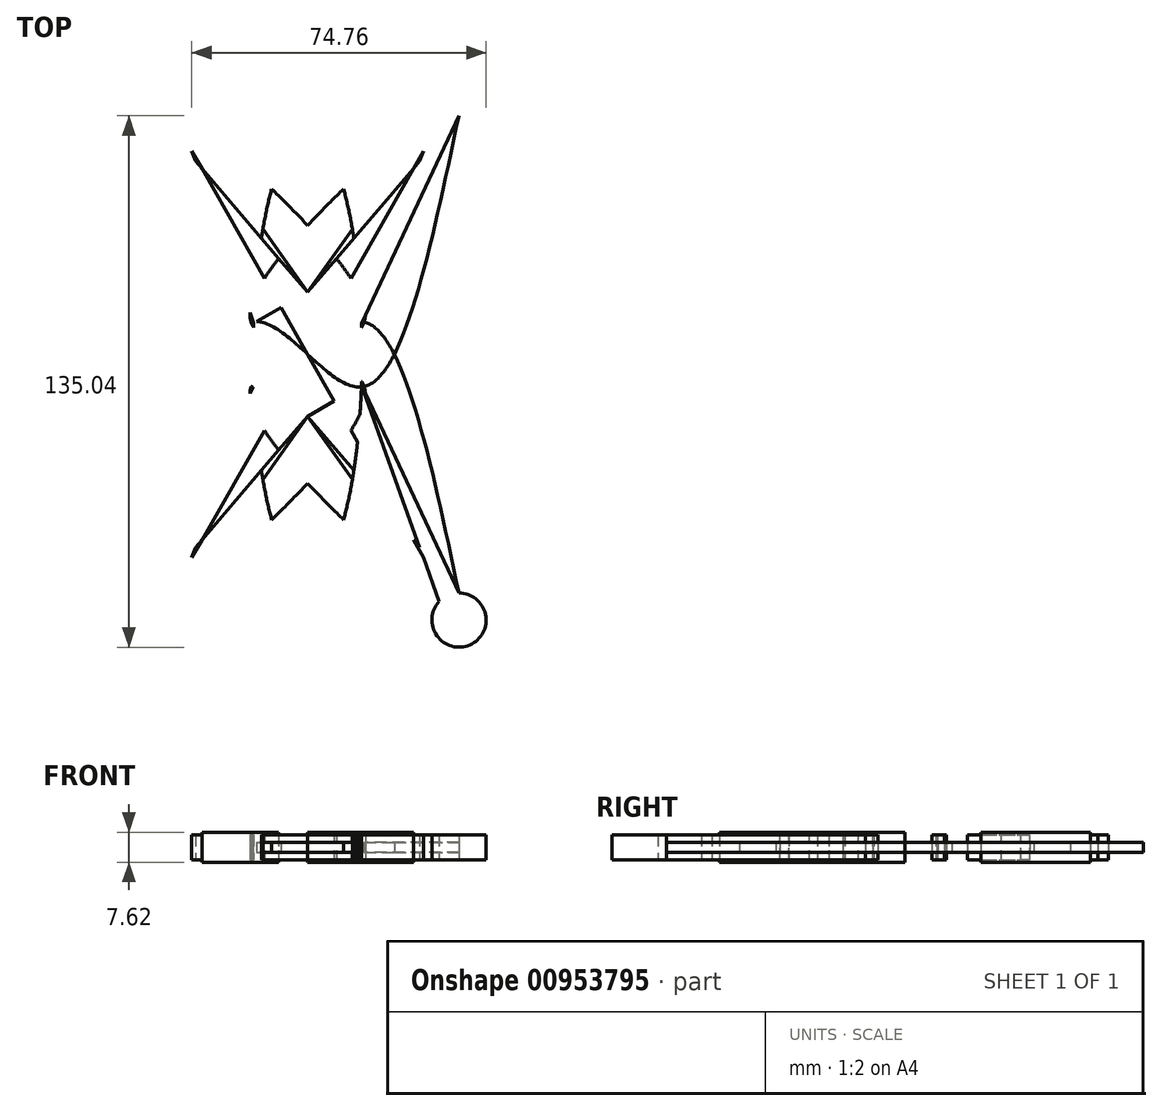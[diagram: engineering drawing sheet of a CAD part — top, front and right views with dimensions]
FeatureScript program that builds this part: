
annotation { "Feature Type Name" : "Feature", "Feature Type Description" : "" }
export const myFeature = defineFeature(function(context is Context, id is Id, definition is map)
    precondition{}
    {
        {
            var Q0;
            Q0=qCreatedBy(makeId("Top.planeOp"),FACE);
            var sketch = newSketch(context, id + "F0", { "sketchPlane" : qUnion([Q0])});
            skEllipse(sketch, "E0", {"center": v(0, 0) * mm, "majorRadius": 55.88 * mm, "minorRadius": 13.83 * mm, "majorAxis": v(0, 1)});
            skCircle(sketch, "E1.cCircle", {"center": v(0, 0) * mm, "radius": 13.7 * mm, "construction": true});
            skLineSegment(sketch, "E1.0", {"start": v(0, 15.8) * mm, "end": v(13.7, 7.9) * mm});
            skLineSegment(sketch, "E1.1", {"start": v(13.7, 7.9) * mm, "end": v(13.7, -7.9) * mm});
            skLineSegment(sketch, "E1.2", {"start": v(13.7, -7.9) * mm, "end": v(0, -15.8) * mm});
            skLineSegment(sketch, "E1.3", {"start": v(0, -15.8) * mm, "end": v(-13.7, -7.9) * mm});
            skLineSegment(sketch, "E1.4", {"start": v(-13.7, -7.9) * mm, "end": v(-13.7, 7.9) * mm});
            skLineSegment(sketch, "E1.5", {"start": v(-13.7, 7.9) * mm, "end": v(0, 15.8) * mm});
            skPoint(sketch, "E1.0.midPoint", {"position": v(6.85, 11.86) * mm});
            skLineSegment(sketch, "E2", {"start": v(0, 15.8) * mm, "end": v(-33.42, 62.8) * mm});
            skLineSegment(sketch, "E3", {"start": v(-13.7, 7.9) * mm, "end": v(-33.42, 62.8) * mm});
            skLineSegment(sketch, "E4", {"start": v(0, 15.8) * mm, "end": v(-38.4, 60.63) * mm});
            skLineSegment(sketch, "E5", {"start": v(-38.4, 60.63) * mm, "end": v(-13.7, 7.9) * mm});
            skLineSegment(sketch, "E6.MirrorCS", {"start": v(38.4, 60.63) * mm, "end": v(13.7, 7.9) * mm});
            skLineSegment(sketch, "E7.MirrorCS", {"start": v(0, 15.8) * mm, "end": v(38.4, 60.63) * mm});
            skLineSegment(sketch, "E8.MirrorCS", {"start": v(13.7, 7.9) * mm, "end": v(33.42, 62.8) * mm});
            skLineSegment(sketch, "E9.MirrorCS", {"start": v(13.7, 7.9) * mm, "end": v(0, 15.8) * mm});
            skLineSegment(sketch, "E10.MirrorCS", {"start": v(0, 15.8) * mm, "end": v(33.42, 62.8) * mm});
            skLineSegment(sketch, "E11.MirrorCS", {"start": v(-13.7, 7.9) * mm, "end": v(-13.7, -7.9) * mm});
            skLineSegment(sketch, "E12.MirrorCS", {"start": v(13.7, -7.9) * mm, "end": v(13.7, 7.9) * mm});
            skLineSegment(sketch, "E13.MirrorCS", {"start": v(0, 15.8) * mm, "end": v(-13.7, 7.9) * mm});
            skPoint(sketch, "E14.MirrorP", {"position": v(-6.85, 11.86) * mm});
            skEllipse(sketch, "E15.MirrorC", {"center": v(0, 0) * mm, "majorRadius": 55.88 * mm, "minorRadius": 13.83 * mm, "majorAxis": v(0, 1)});
            skLineSegment(sketch, "E16.MirrorCS", {"start": v(-13.7, -7.9) * mm, "end": v(0, -15.8) * mm});
            skLineSegment(sketch, "E17.MirrorCS", {"start": v(0, -15.8) * mm, "end": v(-38.4, -60.63) * mm});
            skLineSegment(sketch, "E18.MirrorCS", {"start": v(-13.7, -7.9) * mm, "end": v(-33.42, -62.8) * mm});
            skLineSegment(sketch, "E19.MirrorCS", {"start": v(0, -15.8) * mm, "end": v(-33.42, -62.8) * mm});
            skLineSegment(sketch, "E20.MirrorCS", {"start": v(-38.4, -60.63) * mm, "end": v(-13.7, -7.9) * mm});
            skPoint(sketch, "E21.MirrorP", {"position": v(-6.85, -11.86) * mm});
            skEllipse(sketch, "E22.MirrorC", {"center": v(0, 0) * mm, "majorRadius": 55.88 * mm, "minorRadius": 13.83 * mm, "majorAxis": v(0, -1)});
            skEllipse(sketch, "E23.MirrorC", {"center": v(0, 0) * mm, "majorRadius": 55.88 * mm, "minorRadius": 13.83 * mm, "majorAxis": v(0, -1)});
            skLineSegment(sketch, "E24.MirrorCS", {"start": v(0, -15.8) * mm, "end": v(13.7, -7.9) * mm});
            skLineSegment(sketch, "E25.MirrorCS", {"start": v(13.7, -7.9) * mm, "end": v(33.42, -62.8) * mm});
            skLineSegment(sketch, "E26.MirrorCS", {"start": v(38.4, -60.63) * mm, "end": v(13.7, -7.9) * mm});
            skLineSegment(sketch, "E27.MirrorCS", {"start": v(0, -15.8) * mm, "end": v(33.42, -62.8) * mm});
            skLineSegment(sketch, "E28.MirrorCS", {"start": v(0, -15.8) * mm, "end": v(38.4, -60.63) * mm});
            skPoint(sketch, "E29.MirrorP", {"position": v(6.85, -11.86) * mm});
            skEllipse(sketch, "E30.MirrorC", {"center": v(0, 0) * mm, "majorRadius": 55.88 * mm, "minorRadius": 13.83 * mm, "majorAxis": v(0, -1)});
            skEllipse(sketch, "E31.MirrorC", {"center": v(0, 0) * mm, "majorRadius": 55.88 * mm, "minorRadius": 13.83 * mm, "majorAxis": v(0, 1)});
            skEllipse(sketch, "E32.MirrorC", {"center": v(0, 0) * mm, "majorRadius": 55.88 * mm, "minorRadius": 13.83 * mm, "majorAxis": v(0, -1)});
            skEllipse(sketch, "E33.MirrorC", {"center": v(0, 0) * mm, "majorRadius": 55.88 * mm, "minorRadius": 13.83 * mm, "majorAxis": v(0, 1)});
            skArc(sketch, "E34", {"start": v(-38.4, -60.63) * mm, "mid": v(-41.21, -73.83) * mm, "end": v(-33.42, -62.8) * mm});
            skArc(sketch, "E35.MirrorCS", {"start": v(-38.4, 60.63) * mm, "mid": v(-41.21, 73.83) * mm, "end": v(-33.42, 62.8) * mm});
            skArc(sketch, "E36.MirrorCS", {"start": v(38.4, 60.63) * mm, "mid": v(41.21, 73.83) * mm, "end": v(33.42, 62.8) * mm});
            skArc(sketch, "E37.MirrorCS", {"start": v(38.4, -60.63) * mm, "mid": v(41.21, -73.83) * mm, "end": v(33.42, -62.8) * mm});
            skEllipse(sketch, "E38.MirrorC", {"center": v(0, 0) * mm, "majorRadius": 55.88 * mm, "minorRadius": 13.83 * mm, "majorAxis": v(0, -1)});
            skFitSpline(sketch, "E39", {"points": [v(0, 0) * mm, v(15.27, 7.9) * mm, v(38.4, -60.63) * mm], "startDerivative": vector(48.6, 44.78) * mm, "endDerivative": vector(30.3, -144.32) * mm});
            skFitSpline(sketch, "E40.MirrorCS", {"points": [v(0, 0) * mm, v(15.27, -7.9) * mm, v(38.4, 60.63) * mm], "startDerivative": vector(48.6, -44.78) * mm, "endDerivative": vector(30.3, 144.32) * mm});
            skFitSpline(sketch, "E41.MirrorCS", {"points": [v(0, 0) * mm, v(-15.27, -7.9) * mm, v(-38.4, 60.63) * mm], "startDerivative": vector(-48.6, -44.78) * mm, "endDerivative": vector(-30.3, 144.32) * mm});
            skFitSpline(sketch, "E42.MirrorCS", {"points": [v(0, 0) * mm, v(-15.27, 7.9) * mm, v(-38.4, -60.63) * mm], "startDerivative": vector(-48.6, 44.78) * mm, "endDerivative": vector(-30.3, -144.32) * mm});
            skLineSegment(sketch, "E43", {"start": v(0, 0) * mm, "end": v(-38.45, -67.52) * mm});
            skFitSpline(sketch, "E44.MirrorCS", {"points": [v(0, 0) * mm, v(-15.27, -7.9) * mm, v(-38.4, 60.63) * mm], "startDerivative": vector(-48.6, -44.78) * mm, "endDerivative": vector(-30.3, 144.32) * mm});
            skFitSpline(sketch, "E45.MirrorCS", {"points": [v(0, 0) * mm, v(-15.27, -7.9) * mm, v(-38.4, 60.63) * mm], "startDerivative": vector(-48.6, -44.78) * mm, "endDerivative": vector(-30.3, 144.32) * mm});
            skFitSpline(sketch, "E46.MirrorCS", {"points": [v(0, 0) * mm, v(14.6, -9.1) * mm, v(-32.55, -63.96) * mm], "startDerivative": vector(63.3, -18.95) * mm, "endDerivative": vector(-108.66, -99.7) * mm});
            skLineSegment(sketch, "E47.MirrorCS", {"start": v(0, 0) * mm, "end": v(38.45, -67.52) * mm});
            skFitSpline(sketch, "E48.MirrorCS", {"points": [v(0, 0) * mm, v(-14.6, -9.1) * mm, v(32.55, -63.96) * mm], "startDerivative": vector(-63.3, -18.95) * mm, "endDerivative": vector(108.66, -99.7) * mm});
            skLineSegment(sketch, "E49", {"start": v(0, 0) * mm, "end": v(38.45, 67.52) * mm});
            skLineSegment(sketch, "E50", {"start": v(-38.45, 67.52) * mm, "end": v(0, 0) * mm});
            skFitSpline(sketch, "E51.MirrorCS", {"points": [v(0, 0) * mm, v(-14.6, 9.1) * mm, v(32.55, 63.96) * mm], "startDerivative": vector(-63.3, 18.95) * mm, "endDerivative": vector(108.66, 99.7) * mm});
            skFitSpline(sketch, "E52.MirrorCS", {"points": [v(0, 0) * mm, v(14.6, 9.1) * mm, v(-32.55, 63.96) * mm], "startDerivative": vector(63.3, 18.95) * mm, "endDerivative": vector(-108.66, 99.7) * mm});
            skSolve(sketch);
        }
        {
            var Q0;
            {var subQ0=sQuery(id+"F0.wireOp",EDGE,"E45.MirrorCS");var subQ5=sQuery(id+"F0.wireOp",EDGE,"E42.MirrorCS");var subQ6=makeQuery(id+"F0.imprint","INTERSECT",VERTEX,{"derivedFrom":[subQ5,subQ0]});Q0=makeQuery(id+"F0.imprint","IMPRINT",FACE,{"disambiguationData":[TD([[makeQuery(id+"F0.imprint","IMPRINT",EDGE,{"disambiguationData":[TD([[subQ6,1.0]])],"derivedFrom":subQ5}),-1.0]])]});}
            var Q1;
            {var subQ3=sQuery(id+"F0.wireOp",EDGE,"E38.MirrorC");var subQ5=sQuery(id+"F0.wireOp",EDGE,"E52.MirrorCS");var subQ7=makeQuery(id+"F0.imprint","INTERSECT",VERTEX,{"disambiguationData":[OD(0.0)],"derivedFrom":[subQ3,subQ5]});Q1=makeQuery(id+"F0.imprint","IMPRINT",FACE,{"disambiguationData":[TD([[makeQuery(id+"F0.imprint","IMPRINT",EDGE,{"disambiguationData":[TD([[subQ7,-1.0]])],"derivedFrom":subQ3}),-1.0]])]});}
            var Q2;
            {var subQ3=sQuery(id+"F0.wireOp",EDGE,"E38.MirrorC");var subQ5=sQuery(id+"F0.wireOp",EDGE,"E51.MirrorCS");var subQ7=makeQuery(id+"F0.imprint","INTERSECT",VERTEX,{"disambiguationData":[OD(0.0)],"derivedFrom":[subQ3,subQ5]});Q2=makeQuery(id+"F0.imprint","IMPRINT",FACE,{"disambiguationData":[TD([[makeQuery(id+"F0.imprint","IMPRINT",EDGE,{"disambiguationData":[TD([[subQ7,1.0]])],"derivedFrom":subQ3}),-1.0]])]});}
            var Q3;
            {var subQ0=sQuery(id+"F0.wireOp",EDGE,"E40.MirrorCS");var subQ5=sQuery(id+"F0.wireOp",EDGE,"E39");var subQ6=makeQuery(id+"F0.imprint","INTERSECT",VERTEX,{"derivedFrom":[subQ0,subQ5]});Q3=makeQuery(id+"F0.imprint","IMPRINT",FACE,{"disambiguationData":[TD([[makeQuery(id+"F0.imprint","IMPRINT",EDGE,{"disambiguationData":[TD([[subQ6,1.0]])],"derivedFrom":subQ5}),1.0]])]});}
            var Q4;
            {var subQ0=sQuery(id+"F0.wireOp",EDGE,"E39");var subQ5=sQuery(id+"F0.wireOp",EDGE,"E40.MirrorCS");var subQ6=makeQuery(id+"F0.imprint","INTERSECT",VERTEX,{"derivedFrom":[subQ5,subQ0]});Q4=makeQuery(id+"F0.imprint","IMPRINT",FACE,{"disambiguationData":[TD([[makeQuery(id+"F0.imprint","IMPRINT",EDGE,{"disambiguationData":[TD([[subQ6,1.0]])],"derivedFrom":subQ5}),-1.0]])]});}
            var Q5;
            {var subQ3=sQuery(id+"F0.wireOp",EDGE,"E38.MirrorC");var subQ5=sQuery(id+"F0.wireOp",EDGE,"E48.MirrorCS");var subQ7=makeQuery(id+"F0.imprint","INTERSECT",VERTEX,{"disambiguationData":[OD(0.0)],"derivedFrom":[subQ3,subQ5]});Q5=makeQuery(id+"F0.imprint","IMPRINT",FACE,{"disambiguationData":[TD([[makeQuery(id+"F0.imprint","IMPRINT",EDGE,{"disambiguationData":[TD([[subQ7,-1.0]])],"derivedFrom":subQ3}),-1.0]])]});}
            var Q6;
            {var subQ3=sQuery(id+"F0.wireOp",EDGE,"E38.MirrorC");var subQ5=sQuery(id+"F0.wireOp",EDGE,"E46.MirrorCS");var subQ7=makeQuery(id+"F0.imprint","INTERSECT",VERTEX,{"disambiguationData":[OD(0.0)],"derivedFrom":[subQ3,subQ5]});Q6=makeQuery(id+"F0.imprint","IMPRINT",FACE,{"disambiguationData":[TD([[makeQuery(id+"F0.imprint","IMPRINT",EDGE,{"disambiguationData":[TD([[subQ7,1.0]])],"derivedFrom":subQ3}),-1.0]])]});}
            var Q7;
            {var subQ0=sQuery(id+"F0.wireOp",EDGE,"E42.MirrorCS");var subQ5=sQuery(id+"F0.wireOp",EDGE,"E45.MirrorCS");var subQ6=makeQuery(id+"F0.imprint","INTERSECT",VERTEX,{"derivedFrom":[subQ0,subQ5]});Q7=makeQuery(id+"F0.imprint","IMPRINT",FACE,{"disambiguationData":[TD([[makeQuery(id+"F0.imprint","IMPRINT",EDGE,{"disambiguationData":[TD([[subQ6,1.0]])],"derivedFrom":subQ5}),1.0]])]});}
            var Q8;
            {var subQ0=sQuery(id+"F0.wireOp",EDGE,"E48.MirrorCS");var subQ1=sQuery(id+"F0.wireOp",EDGE,"E38.MirrorC");var subQ2=makeQuery(id+"F0.imprint","INTERSECT",VERTEX,{"disambiguationData":[OD(0.0)],"derivedFrom":[subQ1,subQ0]});Q8=makeQuery(id+"F0.imprint","IMPRINT",FACE,{"disambiguationData":[TD([[makeQuery(id+"F0.imprint","IMPRINT",EDGE,{"disambiguationData":[TD([[subQ2,1.0]])],"derivedFrom":subQ1}),1.0]])]});}
            var Q9;
            {var subQ0=sQuery(id+"F0.wireOp",EDGE,"E51.MirrorCS");var subQ1=sQuery(id+"F0.wireOp",EDGE,"E38.MirrorC");var subQ2=makeQuery(id+"F0.imprint","INTERSECT",VERTEX,{"disambiguationData":[OD(0.0)],"derivedFrom":[subQ1,subQ0]});Q9=makeQuery(id+"F0.imprint","IMPRINT",FACE,{"disambiguationData":[TD([[makeQuery(id+"F0.imprint","IMPRINT",EDGE,{"disambiguationData":[TD([[subQ2,-1.0]])],"derivedFrom":subQ1}),1.0]])]});}
            var Q10;
            {var subQ0=sQuery(id+"F0.wireOp",EDGE,"E51.MirrorCS");var subQ1=sQuery(id+"F0.wireOp",EDGE,"E2");var subQ2=makeQuery(id+"F0.imprint","INTERSECT",VERTEX,{"derivedFrom":[subQ1,subQ0]});Q10=makeQuery(id+"F0.imprint","IMPRINT",FACE,{"disambiguationData":[TD([[makeQuery(id+"F0.imprint","IMPRINT",EDGE,{"disambiguationData":[TD([[subQ2,-1.0]])],"derivedFrom":subQ1}),-1.0]])]});}
            var Q11;
            {var subQ0=sQuery(id+"F0.wireOp",EDGE,"E52.MirrorCS");var subQ1=sQuery(id+"F0.wireOp",EDGE,"E10.MirrorCS");var subQ2=makeQuery(id+"F0.imprint","INTERSECT",VERTEX,{"derivedFrom":[subQ1,subQ0]});Q11=makeQuery(id+"F0.imprint","IMPRINT",FACE,{"disambiguationData":[TD([[makeQuery(id+"F0.imprint","IMPRINT",EDGE,{"disambiguationData":[TD([[subQ2,-1.0]])],"derivedFrom":subQ1}),1.0]])]});}
            var Q12;
            {var subQ0=sQuery(id+"F0.wireOp",EDGE,"E48.MirrorCS");var subQ1=sQuery(id+"F0.wireOp",EDGE,"E19.MirrorCS");var subQ2=makeQuery(id+"F0.imprint","INTERSECT",VERTEX,{"derivedFrom":[subQ1,subQ0]});Q12=makeQuery(id+"F0.imprint","IMPRINT",FACE,{"disambiguationData":[TD([[makeQuery(id+"F0.imprint","IMPRINT",EDGE,{"disambiguationData":[TD([[subQ2,-1.0]])],"derivedFrom":subQ1}),1.0]])]});}
            var Q13;
            {var subQ0=sQuery(id+"F0.wireOp",EDGE,"E46.MirrorCS");var subQ1=sQuery(id+"F0.wireOp",EDGE,"E27.MirrorCS");var subQ2=makeQuery(id+"F0.imprint","INTERSECT",VERTEX,{"derivedFrom":[subQ1,subQ0]});Q13=makeQuery(id+"F0.imprint","IMPRINT",FACE,{"disambiguationData":[TD([[makeQuery(id+"F0.imprint","IMPRINT",EDGE,{"disambiguationData":[TD([[subQ2,-1.0]])],"derivedFrom":subQ1}),-1.0]])]});}
            var Q14;
            {var subQ0=sQuery(id+"F0.wireOp",EDGE,"E27.MirrorCS");var subQ5=sQuery(id+"F0.wireOp",EDGE,"E46.MirrorCS");var subQ6=makeQuery(id+"F0.imprint","INTERSECT",VERTEX,{"derivedFrom":[subQ0,subQ5]});Q14=makeQuery(id+"F0.imprint","IMPRINT",FACE,{"disambiguationData":[TD([[makeQuery(id+"F0.imprint","IMPRINT",EDGE,{"disambiguationData":[TD([[subQ6,-1.0]])],"derivedFrom":subQ5}),-1.0]])]});}
            var Q15;
            {var subQ0=sQuery(id+"F0.wireOp",EDGE,"E2");var subQ5=sQuery(id+"F0.wireOp",EDGE,"E51.MirrorCS");var subQ6=makeQuery(id+"F0.imprint","INTERSECT",VERTEX,{"derivedFrom":[subQ0,subQ5]});Q15=makeQuery(id+"F0.imprint","IMPRINT",FACE,{"disambiguationData":[TD([[makeQuery(id+"F0.imprint","IMPRINT",EDGE,{"disambiguationData":[TD([[subQ6,-1.0]])],"derivedFrom":subQ5}),-1.0]])]});}
            extrude(context, id + "F1", {"entities" : qUnion([Q0, Q1, Q2, Q3, Q4, Q5, Q6, Q7, Q8, Q9, Q10, Q11, Q12, Q13, Q14, Q15]), "endBound" : BoundingType.SYMMETRIC, "depth" : 2.54 * mm, "offsetDistance" : 25.4 * mm});
        }
        {
            var Q0;
            {var subQ4=sQuery(id+"F0.wireOp",EDGE,"E3");var subQ7=makeQuery(id+"F0.imprint","INTERSECT",VERTEX,{"derivedFrom":[subQ4,sQuery(id+"F0.wireOp",EDGE,"E50")]});Q0=makeQuery(id+"F0.imprint","IMPRINT",FACE,{"disambiguationData":[TD([[makeQuery(id+"F0.imprint","IMPRINT",EDGE,{"disambiguationData":[TD([[subQ7,1.0]])],"derivedFrom":subQ4}),1.0]])]});}
            var Q1;
            {var subQ3=sQuery(id+"F0.wireOp",EDGE,"E51.MirrorCS");var subQ5=sQuery(id+"F0.wireOp",EDGE,"E3");var subQ6=makeQuery(id+"F0.imprint","INTERSECT",VERTEX,{"derivedFrom":[subQ5,subQ3]});Q1=makeQuery(id+"F0.imprint","IMPRINT",FACE,{"disambiguationData":[TD([[makeQuery(id+"F0.imprint","IMPRINT",EDGE,{"disambiguationData":[TD([[subQ6,-1.0]])],"derivedFrom":subQ5}),1.0]])]});}
            var Q2;
            {var subQ0=sQuery(id+"F0.wireOp",EDGE,"E38.MirrorC");var subQ1=sQuery(id+"F0.wireOp",EDGE,"E4");var subQ2=makeQuery(id+"F0.imprint","INTERSECT",VERTEX,{"derivedFrom":[subQ1,subQ0]});Q2=makeQuery(id+"F0.imprint","IMPRINT",FACE,{"disambiguationData":[TD([[makeQuery(id+"F0.imprint","IMPRINT",EDGE,{"disambiguationData":[TD([[subQ2,-1.0]])],"derivedFrom":subQ1}),-1.0]])]});}
            var Q3;
            {var subQ3=sQuery(id+"F0.wireOp",EDGE,"E8.MirrorCS");var subQ6=makeQuery(id+"F0.imprint","INTERSECT",VERTEX,{"derivedFrom":[subQ3,sQuery(id+"F0.wireOp",EDGE,"E49")]});Q3=makeQuery(id+"F0.imprint","IMPRINT",FACE,{"disambiguationData":[TD([[makeQuery(id+"F0.imprint","IMPRINT",EDGE,{"disambiguationData":[TD([[subQ6,1.0]])],"derivedFrom":subQ3}),-1.0]])]});}
            var Q4;
            {var subQ0=sQuery(id+"F0.wireOp",EDGE,"E38.MirrorC");var subQ1=sQuery(id+"F0.wireOp",EDGE,"E7.MirrorCS");var subQ2=makeQuery(id+"F0.imprint","INTERSECT",VERTEX,{"derivedFrom":[subQ1,subQ0]});Q4=makeQuery(id+"F0.imprint","IMPRINT",FACE,{"disambiguationData":[TD([[makeQuery(id+"F0.imprint","IMPRINT",EDGE,{"disambiguationData":[TD([[subQ2,-1.0]])],"derivedFrom":subQ1}),1.0]])]});}
            var Q5;
            {var subQ0=sQuery(id+"F0.wireOp",EDGE,"E52.MirrorCS");var subQ1=sQuery(id+"F0.wireOp",EDGE,"E8.MirrorCS");var subQ2=makeQuery(id+"F0.imprint","INTERSECT",VERTEX,{"derivedFrom":[subQ1,subQ0]});Q5=makeQuery(id+"F0.imprint","IMPRINT",FACE,{"disambiguationData":[TD([[makeQuery(id+"F0.imprint","IMPRINT",EDGE,{"disambiguationData":[TD([[subQ2,-1.0]])],"derivedFrom":subQ1}),-1.0]])]});}
            var Q6;
            {var subQ1=sQuery(id+"F0.wireOp",EDGE,"E28.MirrorCS");var subQ3=sQuery(id+"F0.wireOp",EDGE,"E25.MirrorCS");var subQ4=makeQuery(id+"F0.imprint","INTERSECT",VERTEX,{"derivedFrom":[subQ1,subQ3]});Q6=makeQuery(id+"F0.imprint","IMPRINT",FACE,{"disambiguationData":[TD([[makeQuery(id+"F0.imprint","IMPRINT",EDGE,{"disambiguationData":[TD([[subQ4,1.0]])],"derivedFrom":subQ3}),1.0]])]});}
            var Q7;
            {var subQ0=sQuery(id+"F0.wireOp",EDGE,"E38.MirrorC");var subQ1=sQuery(id+"F0.wireOp",EDGE,"E28.MirrorCS");var subQ2=makeQuery(id+"F0.imprint","INTERSECT",VERTEX,{"derivedFrom":[subQ1,subQ0]});Q7=makeQuery(id+"F0.imprint","IMPRINT",FACE,{"disambiguationData":[TD([[makeQuery(id+"F0.imprint","IMPRINT",EDGE,{"disambiguationData":[TD([[subQ2,-1.0]])],"derivedFrom":subQ1}),-1.0]])]});}
            var Q8;
            {var subQ3=sQuery(id+"F0.wireOp",EDGE,"E38.MirrorC");var subQ5=sQuery(id+"F0.wireOp",EDGE,"E17.MirrorCS");var subQ6=makeQuery(id+"F0.imprint","INTERSECT",VERTEX,{"derivedFrom":[subQ5,subQ3]});Q8=makeQuery(id+"F0.imprint","IMPRINT",FACE,{"disambiguationData":[TD([[makeQuery(id+"F0.imprint","IMPRINT",EDGE,{"disambiguationData":[TD([[subQ6,-1.0]])],"derivedFrom":subQ5}),1.0]])]});}
            var Q9;
            {var subQ0=sQuery(id+"F0.wireOp",EDGE,"E48.MirrorCS");var subQ1=sQuery(id+"F0.wireOp",EDGE,"E18.MirrorCS");var subQ2=makeQuery(id+"F0.imprint","INTERSECT",VERTEX,{"derivedFrom":[subQ1,subQ0]});Q9=makeQuery(id+"F0.imprint","IMPRINT",FACE,{"disambiguationData":[TD([[makeQuery(id+"F0.imprint","IMPRINT",EDGE,{"disambiguationData":[TD([[subQ2,-1.0]])],"derivedFrom":subQ1}),-1.0]])]});}
            var Q10;
            {var subQ0=sQuery(id+"F0.wireOp",EDGE,"E43");var subQ1=sQuery(id+"F0.wireOp",EDGE,"E18.MirrorCS");var subQ2=makeQuery(id+"F0.imprint","INTERSECT",VERTEX,{"derivedFrom":[subQ1,subQ0]});Q10=makeQuery(id+"F0.imprint","IMPRINT",FACE,{"disambiguationData":[TD([[makeQuery(id+"F0.imprint","IMPRINT",EDGE,{"disambiguationData":[TD([[subQ2,1.0]])],"derivedFrom":subQ1}),1.0]])]});}
            var Q11;
            {var subQ0=sQuery(id+"F0.wireOp",EDGE,"E48.MirrorCS");var subQ1=sQuery(id+"F0.wireOp",EDGE,"E17.MirrorCS");var subQ2=makeQuery(id+"F0.imprint","INTERSECT",VERTEX,{"derivedFrom":[subQ1,subQ0]});Q11=makeQuery(id+"F0.imprint","IMPRINT",FACE,{"disambiguationData":[TD([[makeQuery(id+"F0.imprint","IMPRINT",EDGE,{"disambiguationData":[TD([[subQ2,-1.0]])],"derivedFrom":subQ1}),1.0]])]});}
            var Q12;
            {var subQ0=sQuery(id+"F0.wireOp",EDGE,"E46.MirrorCS");var subQ1=sQuery(id+"F0.wireOp",EDGE,"E28.MirrorCS");var subQ2=makeQuery(id+"F0.imprint","INTERSECT",VERTEX,{"derivedFrom":[subQ1,subQ0]});Q12=makeQuery(id+"F0.imprint","IMPRINT",FACE,{"disambiguationData":[TD([[makeQuery(id+"F0.imprint","IMPRINT",EDGE,{"disambiguationData":[TD([[subQ2,-1.0]])],"derivedFrom":subQ1}),-1.0]])]});}
            var Q13;
            {var subQ3=sQuery(id+"F0.wireOp",EDGE,"E18.MirrorCS");var subQ6=makeQuery(id+"F0.imprint","INTERSECT",VERTEX,{"derivedFrom":[subQ3,sQuery(id+"F0.wireOp",EDGE,"E43")]});Q13=makeQuery(id+"F0.imprint","IMPRINT",FACE,{"disambiguationData":[TD([[makeQuery(id+"F0.imprint","IMPRINT",EDGE,{"disambiguationData":[TD([[subQ6,1.0]])],"derivedFrom":subQ3}),-1.0]])]});}
            var Q14;
            {var subQ4=sQuery(id+"F0.wireOp",EDGE,"E25.MirrorCS");var subQ5=makeQuery(id+"F0.imprint","INTERSECT",VERTEX,{"derivedFrom":[subQ4,sQuery(id+"F0.wireOp",EDGE,"E47.MirrorCS")]});Q14=makeQuery(id+"F0.imprint","IMPRINT",FACE,{"disambiguationData":[TD([[makeQuery(id+"F0.imprint","IMPRINT",EDGE,{"disambiguationData":[TD([[subQ5,1.0]])],"derivedFrom":subQ4}),1.0]])]});}
            var Q15;
            {var subQ0=sQuery(id+"F0.wireOp",EDGE,"E47.MirrorCS");var subQ1=sQuery(id+"F0.wireOp",EDGE,"E28.MirrorCS");var subQ2=makeQuery(id+"F0.imprint","INTERSECT",VERTEX,{"derivedFrom":[subQ1,subQ0]});Q15=makeQuery(id+"F0.imprint","IMPRINT",FACE,{"disambiguationData":[TD([[makeQuery(id+"F0.imprint","IMPRINT",EDGE,{"disambiguationData":[TD([[subQ2,-1.0]])],"derivedFrom":subQ1}),-1.0]])]});}
            var Q16;
            {var subQ0=sQuery(id+"F0.wireOp",EDGE,"E49");var subQ1=sQuery(id+"F0.wireOp",EDGE,"E8.MirrorCS");var subQ2=makeQuery(id+"F0.imprint","INTERSECT",VERTEX,{"derivedFrom":[subQ1,subQ0]});Q16=makeQuery(id+"F0.imprint","IMPRINT",FACE,{"disambiguationData":[TD([[makeQuery(id+"F0.imprint","IMPRINT",EDGE,{"disambiguationData":[TD([[subQ2,1.0]])],"derivedFrom":subQ1}),1.0]])]});}
            var Q17;
            {var subQ0=sQuery(id+"F0.wireOp",EDGE,"E50");var subQ1=sQuery(id+"F0.wireOp",EDGE,"E3");var subQ2=makeQuery(id+"F0.imprint","INTERSECT",VERTEX,{"derivedFrom":[subQ1,subQ0]});Q17=makeQuery(id+"F0.imprint","IMPRINT",FACE,{"disambiguationData":[TD([[makeQuery(id+"F0.imprint","IMPRINT",EDGE,{"disambiguationData":[TD([[subQ2,1.0]])],"derivedFrom":subQ1}),-1.0]])]});}
            var Q18;
            {var subQ0=sQuery(id+"F0.wireOp",EDGE,"E51.MirrorCS");var subQ1=sQuery(id+"F0.wireOp",EDGE,"E2");var subQ2=makeQuery(id+"F0.imprint","INTERSECT",VERTEX,{"derivedFrom":[subQ1,subQ0]});Q18=makeQuery(id+"F0.imprint","IMPRINT",FACE,{"disambiguationData":[TD([[makeQuery(id+"F0.imprint","IMPRINT",EDGE,{"disambiguationData":[TD([[subQ2,-1.0]])],"derivedFrom":subQ1}),1.0]])]});}
            var Q19;
            {var subQ1=sQuery(id+"F0.wireOp",EDGE,"E2");var subQ3=sQuery(id+"F0.wireOp",EDGE,"E51.MirrorCS");var subQ4=makeQuery(id+"F0.imprint","INTERSECT",VERTEX,{"derivedFrom":[subQ1,subQ3]});Q19=makeQuery(id+"F0.imprint","IMPRINT",FACE,{"disambiguationData":[TD([[makeQuery(id+"F0.imprint","IMPRINT",EDGE,{"disambiguationData":[TD([[subQ4,1.0]])],"derivedFrom":subQ3}),-1.0]])]});}
            var Q20;
            {var subQ0=sQuery(id+"F0.wireOp",EDGE,"E52.MirrorCS");var subQ1=sQuery(id+"F0.wireOp",EDGE,"E7.MirrorCS");var subQ2=makeQuery(id+"F0.imprint","INTERSECT",VERTEX,{"derivedFrom":[subQ1,subQ0]});Q20=makeQuery(id+"F0.imprint","IMPRINT",FACE,{"disambiguationData":[TD([[makeQuery(id+"F0.imprint","IMPRINT",EDGE,{"disambiguationData":[TD([[subQ2,-1.0]])],"derivedFrom":subQ1}),1.0]])]});}
            var Q21;
            {var subQ1=sQuery(id+"F0.wireOp",EDGE,"E7.MirrorCS");var subQ3=sQuery(id+"F0.wireOp",EDGE,"E52.MirrorCS");var subQ4=makeQuery(id+"F0.imprint","INTERSECT",VERTEX,{"derivedFrom":[subQ1,subQ3]});Q21=makeQuery(id+"F0.imprint","IMPRINT",FACE,{"disambiguationData":[TD([[makeQuery(id+"F0.imprint","IMPRINT",EDGE,{"disambiguationData":[TD([[subQ4,-1.0]])],"derivedFrom":subQ3}),1.0]])]});}
            var Q22;
            {var subQ1=sQuery(id+"F0.wireOp",EDGE,"E28.MirrorCS");var subQ3=sQuery(id+"F0.wireOp",EDGE,"E46.MirrorCS");var subQ4=makeQuery(id+"F0.imprint","INTERSECT",VERTEX,{"derivedFrom":[subQ1,subQ3]});Q22=makeQuery(id+"F0.imprint","IMPRINT",FACE,{"disambiguationData":[TD([[makeQuery(id+"F0.imprint","IMPRINT",EDGE,{"disambiguationData":[TD([[subQ4,-1.0]])],"derivedFrom":subQ3}),-1.0]])]});}
            var Q23;
            {var subQ1=sQuery(id+"F0.wireOp",EDGE,"E17.MirrorCS");var subQ3=sQuery(id+"F0.wireOp",EDGE,"E48.MirrorCS");var subQ4=makeQuery(id+"F0.imprint","INTERSECT",VERTEX,{"derivedFrom":[subQ1,subQ3]});Q23=makeQuery(id+"F0.imprint","IMPRINT",FACE,{"disambiguationData":[TD([[makeQuery(id+"F0.imprint","IMPRINT",EDGE,{"disambiguationData":[TD([[subQ4,-1.0]])],"derivedFrom":subQ3}),1.0]])]});}
            var Q24;
            {var subQ1=sQuery(id+"F0.wireOp",EDGE,"E38.MirrorC");var subQ7=sQuery(id+"F0.wireOp",EDGE,"E51.MirrorCS");var subQ9=makeQuery(id+"F0.imprint","INTERSECT",VERTEX,{"disambiguationData":[OD(2.0)],"derivedFrom":[subQ1,subQ7]});Q24=makeQuery(id+"F0.imprint","IMPRINT",FACE,{"disambiguationData":[TD([[makeQuery(id+"F0.imprint","IMPRINT",EDGE,{"disambiguationData":[TD([[subQ9,-1.0]])],"derivedFrom":subQ1}),-1.0]])]});}
            var Q25;
            {var subQ5=sQuery(id+"F0.wireOp",EDGE,"E46.MirrorCS");var subQ6=sQuery(id+"F0.wireOp",EDGE,"E38.MirrorC");var subQ7=makeQuery(id+"F0.imprint","INTERSECT",VERTEX,{"disambiguationData":[OD(2.0)],"derivedFrom":[subQ6,subQ5]});Q25=makeQuery(id+"F0.imprint","IMPRINT",FACE,{"disambiguationData":[TD([[makeQuery(id+"F0.imprint","IMPRINT",EDGE,{"disambiguationData":[TD([[subQ7,-1.0]])],"derivedFrom":subQ6}),-1.0]])]});}
            var Q26;
            {var subQ1=sQuery(id+"F0.wireOp",EDGE,"E6.MirrorCS");var subQ3=sQuery(id+"F0.wireOp",EDGE,"E39");var subQ4=makeQuery(id+"F0.imprint","INTERSECT",VERTEX,{"derivedFrom":[subQ1,subQ3]});Q26=makeQuery(id+"F0.imprint","IMPRINT",FACE,{"disambiguationData":[TD([[makeQuery(id+"F0.imprint","IMPRINT",EDGE,{"disambiguationData":[TD([[subQ4,-1.0]])],"derivedFrom":subQ3}),-1.0]])]});}
            var Q27;
            {var subQ0=sQuery(id+"F0.wireOp",EDGE,"E52.MirrorCS");var subQ1=sQuery(id+"F0.wireOp",EDGE,"E6.MirrorCS");var subQ2=makeQuery(id+"F0.imprint","INTERSECT",VERTEX,{"derivedFrom":[subQ1,subQ0]});Q27=makeQuery(id+"F0.imprint","IMPRINT",FACE,{"disambiguationData":[TD([[makeQuery(id+"F0.imprint","IMPRINT",EDGE,{"disambiguationData":[TD([[subQ2,-1.0]])],"derivedFrom":subQ1}),1.0]])]});}
            var Q28;
            {var subQ0=sQuery(id+"F0.wireOp",EDGE,"E39");var subQ1=sQuery(id+"F0.wireOp",EDGE,"E8.MirrorCS");var subQ2=makeQuery(id+"F0.imprint","INTERSECT",VERTEX,{"derivedFrom":[subQ1,subQ0]});Q28=makeQuery(id+"F0.imprint","IMPRINT",FACE,{"disambiguationData":[TD([[makeQuery(id+"F0.imprint","IMPRINT",EDGE,{"disambiguationData":[TD([[subQ2,-1.0]])],"derivedFrom":subQ1}),-1.0]])]});}
            var Q29;
            {var subQ1=sQuery(id+"F0.wireOp",EDGE,"E5");var subQ3=sQuery(id+"F0.wireOp",EDGE,"E42.MirrorCS");var subQ4=makeQuery(id+"F0.imprint","INTERSECT",VERTEX,{"derivedFrom":[subQ1,subQ3]});Q29=makeQuery(id+"F0.imprint","IMPRINT",FACE,{"disambiguationData":[TD([[makeQuery(id+"F0.imprint","IMPRINT",EDGE,{"disambiguationData":[TD([[subQ4,-1.0]])],"derivedFrom":subQ3}),1.0]])]});}
            var Q30;
            {var subQ0=sQuery(id+"F0.wireOp",EDGE,"E51.MirrorCS");var subQ1=sQuery(id+"F0.wireOp",EDGE,"E5");var subQ2=makeQuery(id+"F0.imprint","INTERSECT",VERTEX,{"derivedFrom":[subQ1,subQ0]});Q30=makeQuery(id+"F0.imprint","IMPRINT",FACE,{"disambiguationData":[TD([[makeQuery(id+"F0.imprint","IMPRINT",EDGE,{"disambiguationData":[TD([[subQ2,-1.0]])],"derivedFrom":subQ1}),-1.0]])]});}
            var Q31;
            {var subQ0=sQuery(id+"F0.wireOp",EDGE,"E51.MirrorCS");var subQ1=sQuery(id+"F0.wireOp",EDGE,"E5");var subQ2=makeQuery(id+"F0.imprint","INTERSECT",VERTEX,{"derivedFrom":[subQ1,subQ0]});Q31=makeQuery(id+"F0.imprint","IMPRINT",FACE,{"disambiguationData":[TD([[makeQuery(id+"F0.imprint","IMPRINT",EDGE,{"disambiguationData":[TD([[subQ2,-1.0]])],"derivedFrom":subQ1}),1.0]])]});}
            var Q32;
            {var subQ0=sQuery(id+"F0.wireOp",EDGE,"E45.MirrorCS");var subQ1=sQuery(id+"F0.wireOp",EDGE,"E18.MirrorCS");var subQ2=makeQuery(id+"F0.imprint","INTERSECT",VERTEX,{"derivedFrom":[subQ1,subQ0]});Q32=makeQuery(id+"F0.imprint","IMPRINT",FACE,{"disambiguationData":[TD([[makeQuery(id+"F0.imprint","IMPRINT",EDGE,{"disambiguationData":[TD([[subQ2,-1.0]])],"derivedFrom":subQ1}),-1.0]])]});}
            var Q33;
            {var subQ0=sQuery(id+"F0.wireOp",EDGE,"E48.MirrorCS");var subQ1=sQuery(id+"F0.wireOp",EDGE,"E20.MirrorCS");var subQ2=makeQuery(id+"F0.imprint","INTERSECT",VERTEX,{"derivedFrom":[subQ1,subQ0]});Q33=makeQuery(id+"F0.imprint","IMPRINT",FACE,{"disambiguationData":[TD([[makeQuery(id+"F0.imprint","IMPRINT",EDGE,{"disambiguationData":[TD([[subQ2,-1.0]])],"derivedFrom":subQ1}),1.0]])]});}
            var Q34;
            {var subQ1=sQuery(id+"F0.wireOp",EDGE,"E20.MirrorCS");var subQ3=sQuery(id+"F0.wireOp",EDGE,"E45.MirrorCS");var subQ4=makeQuery(id+"F0.imprint","INTERSECT",VERTEX,{"derivedFrom":[subQ1,subQ3]});Q34=makeQuery(id+"F0.imprint","IMPRINT",FACE,{"disambiguationData":[TD([[makeQuery(id+"F0.imprint","IMPRINT",EDGE,{"disambiguationData":[TD([[subQ4,-1.0]])],"derivedFrom":subQ3}),-1.0]])]});}
            var Q35;
            {var subQ0=sQuery(id+"F0.wireOp",EDGE,"E46.MirrorCS");var subQ1=sQuery(id+"F0.wireOp",EDGE,"E26.MirrorCS");var subQ2=makeQuery(id+"F0.imprint","INTERSECT",VERTEX,{"derivedFrom":[subQ1,subQ0]});Q35=makeQuery(id+"F0.imprint","IMPRINT",FACE,{"disambiguationData":[TD([[makeQuery(id+"F0.imprint","IMPRINT",EDGE,{"disambiguationData":[TD([[subQ2,-1.0]])],"derivedFrom":subQ1}),-1.0]])]});}
            var Q36;
            {var subQ1=sQuery(id+"F0.wireOp",EDGE,"E26.MirrorCS");var subQ3=sQuery(id+"F0.wireOp",EDGE,"E40.MirrorCS");var subQ4=makeQuery(id+"F0.imprint","INTERSECT",VERTEX,{"derivedFrom":[subQ1,subQ3]});Q36=makeQuery(id+"F0.imprint","IMPRINT",FACE,{"disambiguationData":[TD([[makeQuery(id+"F0.imprint","IMPRINT",EDGE,{"disambiguationData":[TD([[subQ4,-1.0]])],"derivedFrom":subQ3}),1.0]])]});}
            var Q37;
            {var subQ0=sQuery(id+"F0.wireOp",EDGE,"E40.MirrorCS");var subQ1=sQuery(id+"F0.wireOp",EDGE,"E25.MirrorCS");var subQ2=makeQuery(id+"F0.imprint","INTERSECT",VERTEX,{"derivedFrom":[subQ1,subQ0]});Q37=makeQuery(id+"F0.imprint","IMPRINT",FACE,{"disambiguationData":[TD([[makeQuery(id+"F0.imprint","IMPRINT",EDGE,{"disambiguationData":[TD([[subQ2,-1.0]])],"derivedFrom":subQ1}),1.0]])]});}
            var Q38;
            {var subQ1=sQuery(id+"F0.wireOp",EDGE,"E25.MirrorCS");var subQ3=sQuery(id+"F0.wireOp",EDGE,"E40.MirrorCS");var subQ4=makeQuery(id+"F0.imprint","INTERSECT",VERTEX,{"derivedFrom":[subQ1,subQ3]});Q38=makeQuery(id+"F0.imprint","IMPRINT",FACE,{"disambiguationData":[TD([[makeQuery(id+"F0.imprint","IMPRINT",EDGE,{"disambiguationData":[TD([[subQ4,-1.0]])],"derivedFrom":subQ3}),1.0]])]});}
            var Q39;
            {var subQ1=sQuery(id+"F0.wireOp",EDGE,"E18.MirrorCS");var subQ3=sQuery(id+"F0.wireOp",EDGE,"E45.MirrorCS");var subQ4=makeQuery(id+"F0.imprint","INTERSECT",VERTEX,{"derivedFrom":[subQ1,subQ3]});Q39=makeQuery(id+"F0.imprint","IMPRINT",FACE,{"disambiguationData":[TD([[makeQuery(id+"F0.imprint","IMPRINT",EDGE,{"disambiguationData":[TD([[subQ4,-1.0]])],"derivedFrom":subQ3}),-1.0]])]});}
            extrude(context, id + "F2", {"entities" : qUnion([Q0, Q1, Q2, Q3, Q4, Q5, Q6, Q7, Q8, Q9, Q10, Q11, Q12, Q13, Q14, Q15, Q16, Q17, Q18, Q19, Q20, Q21, Q22, Q23, Q24, Q25, Q26, Q27, Q28, Q29, Q30, Q31, Q32, Q33, Q34, Q35, Q36, Q37, Q38, Q39]), "endBound" : BoundingType.SYMMETRIC, "depth" : 6.35 * mm, "offsetDistance" : 25.4 * mm});
        }
        {
            var Q0;
            {var subQ0=sQuery(id+"F0.wireOp",EDGE,"E9.MirrorCS");var subQ5=sQuery(id+"F0.wireOp",EDGE,"E49");var subQ6=makeQuery(id+"F0.imprint","INTERSECT",VERTEX,{"derivedFrom":[subQ0,subQ5]});Q0=makeQuery(id+"F0.imprint","IMPRINT",FACE,{"disambiguationData":[TD([[makeQuery(id+"F0.imprint","IMPRINT",EDGE,{"disambiguationData":[TD([[subQ6,-1.0]])],"derivedFrom":subQ5}),1.0]])]});}
            var Q1;
            {var subQ1=sQuery(id+"F0.wireOp",EDGE,"E9.MirrorCS");var subQ5=sQuery(id+"F0.wireOp",EDGE,"E39");var subQ6=makeQuery(id+"F0.imprint","INTERSECT",VERTEX,{"derivedFrom":[subQ1,subQ5]});Q1=makeQuery(id+"F0.imprint","IMPRINT",FACE,{"disambiguationData":[TD([[makeQuery(id+"F0.imprint","IMPRINT",EDGE,{"disambiguationData":[TD([[subQ6,-1.0]])],"derivedFrom":subQ1}),-1.0]])]});}
            var Q2;
            {var subQ1=sQuery(id+"F0.wireOp",EDGE,"E9.MirrorCS");var subQ3=sQuery(id+"F0.wireOp",EDGE,"E49");var subQ4=makeQuery(id+"F0.imprint","INTERSECT",VERTEX,{"derivedFrom":[subQ1,subQ3]});Q2=makeQuery(id+"F0.imprint","IMPRINT",FACE,{"disambiguationData":[TD([[makeQuery(id+"F0.imprint","IMPRINT",EDGE,{"disambiguationData":[TD([[subQ4,-1.0]])],"derivedFrom":subQ1}),1.0]])]});}
            var Q3;
            {var subQ0=sQuery(id+"F0.wireOp",EDGE,"E39");var subQ1=sQuery(id+"F0.wireOp",EDGE,"E9.MirrorCS");var subQ2=makeQuery(id+"F0.imprint","INTERSECT",VERTEX,{"derivedFrom":[subQ1,subQ0]});Q3=makeQuery(id+"F0.imprint","IMPRINT",FACE,{"disambiguationData":[TD([[makeQuery(id+"F0.imprint","IMPRINT",EDGE,{"disambiguationData":[TD([[subQ2,-1.0]])],"derivedFrom":subQ1}),1.0]])]});}
            var Q4;
            {var subQ0=sQuery(id+"F0.wireOp",EDGE,"E42.MirrorCS");var subQ1=sQuery(id+"F0.wireOp",EDGE,"E1.5");var subQ2=makeQuery(id+"F0.imprint","INTERSECT",VERTEX,{"derivedFrom":[subQ1,subQ0]});Q4=makeQuery(id+"F0.imprint","IMPRINT",FACE,{"disambiguationData":[TD([[makeQuery(id+"F0.imprint","IMPRINT",EDGE,{"disambiguationData":[TD([[subQ2,-1.0]])],"derivedFrom":subQ1}),-1.0]])]});}
            var Q5;
            {var subQ0=sQuery(id+"F0.wireOp",EDGE,"E51.MirrorCS");var subQ1=sQuery(id+"F0.wireOp",EDGE,"E11.MirrorCS");var subQ2=makeQuery(id+"F0.imprint","INTERSECT",VERTEX,{"derivedFrom":[subQ1,subQ0]});Q5=makeQuery(id+"F0.imprint","IMPRINT",FACE,{"disambiguationData":[TD([[makeQuery(id+"F0.imprint","IMPRINT",EDGE,{"disambiguationData":[TD([[subQ2,-1.0]])],"derivedFrom":subQ1}),1.0]])]});}
            var Q6;
            {var subQ0=sQuery(id+"F0.wireOp",EDGE,"E45.MirrorCS");var subQ1=sQuery(id+"F0.wireOp",EDGE,"E16.MirrorCS");var subQ2=makeQuery(id+"F0.imprint","INTERSECT",VERTEX,{"derivedFrom":[subQ1,subQ0]});Q6=makeQuery(id+"F0.imprint","IMPRINT",FACE,{"disambiguationData":[TD([[makeQuery(id+"F0.imprint","IMPRINT",EDGE,{"disambiguationData":[TD([[subQ2,-1.0]])],"derivedFrom":subQ1}),1.0]])]});}
            var Q7;
            {var subQ1=sQuery(id+"F0.wireOp",EDGE,"E16.MirrorCS");var subQ3=sQuery(id+"F0.wireOp",EDGE,"E43");var subQ4=makeQuery(id+"F0.imprint","INTERSECT",VERTEX,{"derivedFrom":[subQ1,subQ3]});Q7=makeQuery(id+"F0.imprint","IMPRINT",FACE,{"disambiguationData":[TD([[makeQuery(id+"F0.imprint","IMPRINT",EDGE,{"disambiguationData":[TD([[subQ4,-1.0]])],"derivedFrom":subQ1}),1.0]])]});}
            var Q8;
            {var subQ0=sQuery(id+"F0.wireOp",EDGE,"E40.MirrorCS");var subQ1=sQuery(id+"F0.wireOp",EDGE,"E1.2");var subQ2=makeQuery(id+"F0.imprint","INTERSECT",VERTEX,{"derivedFrom":[subQ1,subQ0]});Q8=makeQuery(id+"F0.imprint","IMPRINT",FACE,{"disambiguationData":[TD([[makeQuery(id+"F0.imprint","IMPRINT",EDGE,{"disambiguationData":[TD([[subQ2,-1.0]])],"derivedFrom":subQ1}),-1.0]])]});}
            var Q9;
            {var subQ0=sQuery(id+"F0.wireOp",EDGE,"E46.MirrorCS");var subQ1=sQuery(id+"F0.wireOp",EDGE,"E12.MirrorCS");var subQ2=makeQuery(id+"F0.imprint","INTERSECT",VERTEX,{"derivedFrom":[subQ1,subQ0]});Q9=makeQuery(id+"F0.imprint","IMPRINT",FACE,{"disambiguationData":[TD([[makeQuery(id+"F0.imprint","IMPRINT",EDGE,{"disambiguationData":[TD([[subQ2,-1.0]])],"derivedFrom":subQ1}),1.0]])]});}
            var Q10;
            {var subQ1=sQuery(id+"F0.wireOp",EDGE,"E16.MirrorCS");var subQ3=sQuery(id+"F0.wireOp",EDGE,"E43");var subQ4=makeQuery(id+"F0.imprint","INTERSECT",VERTEX,{"derivedFrom":[subQ1,subQ3]});Q10=makeQuery(id+"F0.imprint","IMPRINT",FACE,{"disambiguationData":[TD([[makeQuery(id+"F0.imprint","IMPRINT",EDGE,{"disambiguationData":[TD([[subQ4,-1.0]])],"derivedFrom":subQ3}),1.0]])]});}
            var Q11;
            {var subQ0=sQuery(id+"F0.wireOp",EDGE,"E28.MirrorCS");var subQ5=sQuery(id+"F0.wireOp",EDGE,"E46.MirrorCS");var subQ6=makeQuery(id+"F0.imprint","INTERSECT",VERTEX,{"derivedFrom":[subQ0,subQ5]});Q11=makeQuery(id+"F0.imprint","IMPRINT",FACE,{"disambiguationData":[TD([[makeQuery(id+"F0.imprint","IMPRINT",EDGE,{"disambiguationData":[TD([[subQ6,1.0]])],"derivedFrom":subQ5}),-1.0]])]});}
            var Q12;
            {var subQ0=sQuery(id+"F0.wireOp",EDGE,"E48.MirrorCS");var subQ1=sQuery(id+"F0.wireOp",EDGE,"E17.MirrorCS");var subQ2=makeQuery(id+"F0.imprint","INTERSECT",VERTEX,{"derivedFrom":[subQ1,subQ0]});Q12=makeQuery(id+"F0.imprint","IMPRINT",FACE,{"disambiguationData":[TD([[makeQuery(id+"F0.imprint","IMPRINT",EDGE,{"disambiguationData":[TD([[subQ2,-1.0]])],"derivedFrom":subQ1}),-1.0]])]});}
            var Q13;
            {var subQ0=sQuery(id+"F0.wireOp",EDGE,"E46.MirrorCS");var subQ1=sQuery(id+"F0.wireOp",EDGE,"E28.MirrorCS");var subQ2=makeQuery(id+"F0.imprint","INTERSECT",VERTEX,{"derivedFrom":[subQ1,subQ0]});Q13=makeQuery(id+"F0.imprint","IMPRINT",FACE,{"disambiguationData":[TD([[makeQuery(id+"F0.imprint","IMPRINT",EDGE,{"disambiguationData":[TD([[subQ2,-1.0]])],"derivedFrom":subQ1}),1.0]])]});}
            var Q14;
            {var subQ5=sQuery(id+"F0.wireOp",EDGE,"E40.MirrorCS");var subQ6=sQuery(id+"F0.wireOp",EDGE,"E1.2");var subQ7=makeQuery(id+"F0.imprint","INTERSECT",VERTEX,{"derivedFrom":[subQ6,subQ5]});Q14=makeQuery(id+"F0.imprint","IMPRINT",FACE,{"disambiguationData":[TD([[makeQuery(id+"F0.imprint","IMPRINT",EDGE,{"disambiguationData":[TD([[subQ7,-1.0]])],"derivedFrom":subQ6}),1.0]])]});}
            var Q15;
            {var subQ1=sQuery(id+"F0.wireOp",EDGE,"E16.MirrorCS");var subQ5=sQuery(id+"F0.wireOp",EDGE,"E45.MirrorCS");var subQ6=makeQuery(id+"F0.imprint","INTERSECT",VERTEX,{"derivedFrom":[subQ1,subQ5]});Q15=makeQuery(id+"F0.imprint","IMPRINT",FACE,{"disambiguationData":[TD([[makeQuery(id+"F0.imprint","IMPRINT",EDGE,{"disambiguationData":[TD([[subQ6,-1.0]])],"derivedFrom":subQ1}),-1.0]])]});}
            var Q16;
            {var subQ1=sQuery(id+"F0.wireOp",EDGE,"E1.5");var subQ5=sQuery(id+"F0.wireOp",EDGE,"E42.MirrorCS");var subQ6=makeQuery(id+"F0.imprint","INTERSECT",VERTEX,{"derivedFrom":[subQ1,subQ5]});Q16=makeQuery(id+"F0.imprint","IMPRINT",FACE,{"disambiguationData":[TD([[makeQuery(id+"F0.imprint","IMPRINT",EDGE,{"disambiguationData":[TD([[subQ6,-1.0]])],"derivedFrom":subQ1}),1.0]])]});}
            var Q17;
            {var subQ1=sQuery(id+"F0.wireOp",EDGE,"E1.5");var subQ3=sQuery(id+"F0.wireOp",EDGE,"E50");var subQ4=makeQuery(id+"F0.imprint","INTERSECT",VERTEX,{"derivedFrom":[subQ1,subQ3]});Q17=makeQuery(id+"F0.imprint","IMPRINT",FACE,{"disambiguationData":[TD([[makeQuery(id+"F0.imprint","IMPRINT",EDGE,{"disambiguationData":[TD([[subQ4,1.0]])],"derivedFrom":subQ3}),1.0]])]});}
            var Q18;
            {var subQ0=sQuery(id+"F0.wireOp",EDGE,"E51.MirrorCS");var subQ1=sQuery(id+"F0.wireOp",EDGE,"E4");var subQ2=makeQuery(id+"F0.imprint","INTERSECT",VERTEX,{"derivedFrom":[subQ1,subQ0]});Q18=makeQuery(id+"F0.imprint","IMPRINT",FACE,{"disambiguationData":[TD([[makeQuery(id+"F0.imprint","IMPRINT",EDGE,{"disambiguationData":[TD([[subQ2,-1.0]])],"derivedFrom":subQ1}),1.0]])]});}
            var Q19;
            {var subQ0=sQuery(id+"F0.wireOp",EDGE,"E50");var subQ1=sQuery(id+"F0.wireOp",EDGE,"E38.MirrorC");var subQ2=makeQuery(id+"F0.imprint","INTERSECT",VERTEX,{"derivedFrom":[subQ1,subQ0]});Q19=makeQuery(id+"F0.imprint","IMPRINT",FACE,{"disambiguationData":[TD([[makeQuery(id+"F0.imprint","IMPRINT",EDGE,{"disambiguationData":[TD([[subQ2,-1.0]])],"derivedFrom":subQ1}),1.0]])]});}
            var Q20;
            {var subQ0=sQuery(id+"F0.wireOp",EDGE,"E52.MirrorCS");var subQ1=sQuery(id+"F0.wireOp",EDGE,"E7.MirrorCS");var subQ2=makeQuery(id+"F0.imprint","INTERSECT",VERTEX,{"derivedFrom":[subQ1,subQ0]});Q20=makeQuery(id+"F0.imprint","IMPRINT",FACE,{"disambiguationData":[TD([[makeQuery(id+"F0.imprint","IMPRINT",EDGE,{"disambiguationData":[TD([[subQ2,-1.0]])],"derivedFrom":subQ1}),-1.0]])]});}
            var Q21;
            {var subQ0=sQuery(id+"F0.wireOp",EDGE,"E52.MirrorCS");var subQ1=sQuery(id+"F0.wireOp",EDGE,"E38.MirrorC");var subQ2=makeQuery(id+"F0.imprint","INTERSECT",VERTEX,{"disambiguationData":[OD(2.0)],"derivedFrom":[subQ1,subQ0]});Q21=makeQuery(id+"F0.imprint","IMPRINT",FACE,{"disambiguationData":[TD([[makeQuery(id+"F0.imprint","IMPRINT",EDGE,{"disambiguationData":[TD([[subQ2,-1.0]])],"derivedFrom":subQ1}),1.0]])]});}
            var Q22;
            {var subQ0=sQuery(id+"F0.wireOp",EDGE,"E47.MirrorCS");var subQ1=sQuery(id+"F0.wireOp",EDGE,"E38.MirrorC");var subQ2=makeQuery(id+"F0.imprint","INTERSECT",VERTEX,{"derivedFrom":[subQ1,subQ0]});Q22=makeQuery(id+"F0.imprint","IMPRINT",FACE,{"disambiguationData":[TD([[makeQuery(id+"F0.imprint","IMPRINT",EDGE,{"disambiguationData":[TD([[subQ2,-1.0]])],"derivedFrom":subQ1}),1.0]])]});}
            var Q23;
            {var subQ0=sQuery(id+"F0.wireOp",EDGE,"E48.MirrorCS");var subQ1=sQuery(id+"F0.wireOp",EDGE,"E38.MirrorC");var subQ2=makeQuery(id+"F0.imprint","INTERSECT",VERTEX,{"disambiguationData":[OD(2.0)],"derivedFrom":[subQ1,subQ0]});Q23=makeQuery(id+"F0.imprint","IMPRINT",FACE,{"disambiguationData":[TD([[makeQuery(id+"F0.imprint","IMPRINT",EDGE,{"disambiguationData":[TD([[subQ2,-1.0]])],"derivedFrom":subQ1}),1.0]])]});}
            extrude(context, id + "F3", {"entities" : qUnion([Q0, Q1, Q2, Q3, Q4, Q5, Q6, Q7, Q8, Q9, Q10, Q11, Q12, Q13, Q14, Q15, Q16, Q17, Q18, Q19, Q20, Q21, Q22, Q23]), "endBound" : BoundingType.SYMMETRIC, "depth" : 7.62 * mm, "offsetDistance" : 25.4 * mm});
        }
    });
